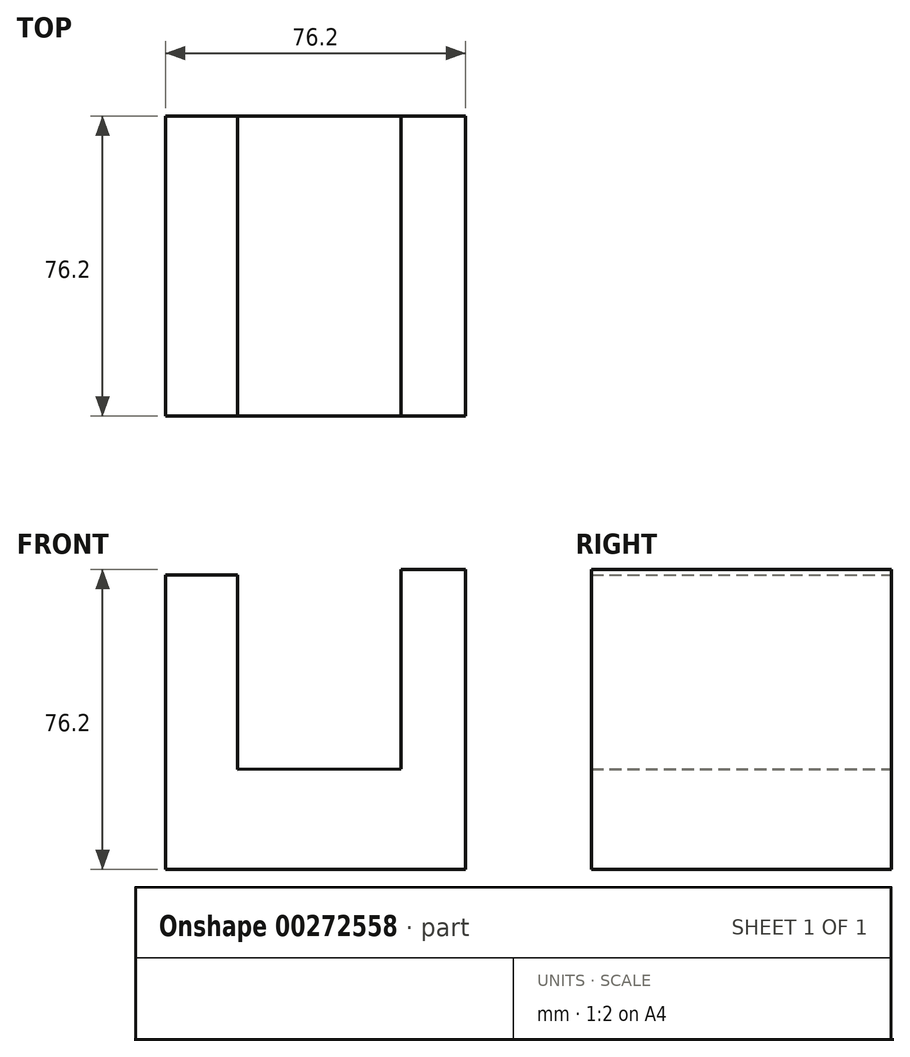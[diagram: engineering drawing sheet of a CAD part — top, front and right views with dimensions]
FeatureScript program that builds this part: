
annotation { "Feature Type Name" : "Feature", "Feature Type Description" : "" }
export const myFeature = defineFeature(function(context is Context, id is Id, definition is map)
    precondition{}
    {
        {
            var Q0;
            Q0=qCreatedBy(makeId("Front.planeOp"),FACE);
            var sketch = newSketch(context, id + "F0", { "sketchPlane" : qUnion([Q0])});
            skLineSegment(sketch, "E0", {"start": v(-50.8, -32.84) * mm, "end": v(25.4, -32.84) * mm});
            skLineSegment(sketch, "E1", {"start": v(25.4, -32.84) * mm, "end": v(25.4, 43.36) * mm});
            skLineSegment(sketch, "E2", {"start": v(-32.46, -7.44) * mm, "end": v(-32.46, 42.01) * mm});
            skLineSegment(sketch, "E3", {"start": v(-50.8, -32.84) * mm, "end": v(-50.8, 42.01) * mm});
            skLineSegment(sketch, "E4", {"start": v(-50.8, 42.01) * mm, "end": v(-32.46, 42.01) * mm});
            skLineSegment(sketch, "E5", {"start": v(25.4, 43.36) * mm, "end": v(8.97, 43.36) * mm});
            skLineSegment(sketch, "E6", {"start": v(8.97, 43.36) * mm, "end": v(8.97, -7.26) * mm});
            skLineSegment(sketch, "E7", {"start": v(8.97, -7.26) * mm, "end": v(-32.46, -7.44) * mm});
            skSolve(sketch);
        }
        {
            var Q0;
            Q0=makeQuery(id+"F0.imprint","IMPRINT",FACE,{"disambiguationData":[TD([[makeQuery(id+"F0.imprint","IMPRINT",EDGE,{"derivedFrom":sQuery(id+"F0.wireOp",EDGE,"E0")}),1.0]])]});
            extrude(context, id + "F1", {"entities" : qUnion([Q0]), "depth" : 76.2 * mm});
        }
    });
